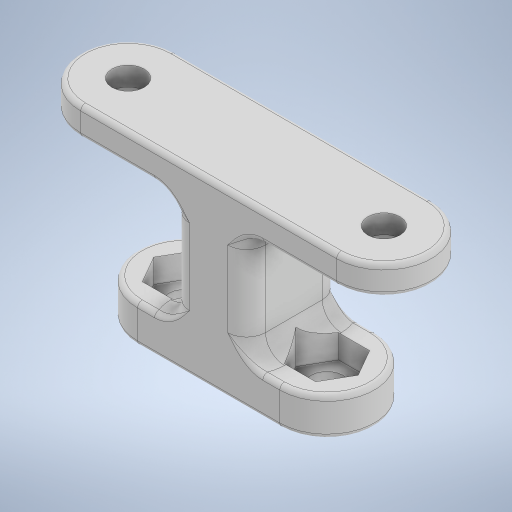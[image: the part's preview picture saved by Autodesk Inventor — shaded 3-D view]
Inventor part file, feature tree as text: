
AUTODESK INVENTOR PART (.ipt)
format: ipt  version: 2024.2 (Build 282272000, 272)  size: 422,912 bytes
history: native  units: mm
features: extrude x6, sketch x6, fillet x2
ambient origin geometry x8: Origin, YZ Plane, XZ Plane, XY Plane, X Axis, Y Axis, Z Axis, Center Point
bodies: Solid1 (feature_tree)
feature tree (14):
  extrude  "Extrusion1"  Depth=27.0mm
  extrude  "Extrusion2"  Depth=10.0mm TaperAngle=0.0deg
  extrude  "Extrusion3"  Depth=15.0mm
  extrude  "Extrusion4"  Depth=5.7mm
  extrude  "Extrusion5"  Depth=3.4mm
  extrude  "Extrusion6"  Depth=0.5mm
  fillet  "Fillet3"  Radius=1.0mm
  fillet  "Fillet2"  Radius=0.5mm
  sketch  "Sketch1"  dims[d0=3.4mm d1=27.0mm]
  sketch  "Sketch2"  dims[d2=10.0mm d3=3.0mm d4=0.0mm]
  sketch  "Sketch3"  dims[d5=12.0mm d6=0.0mm d7=15.0mm]
  sketch  "Sketch4"  dims[d8=4.0mm d9=0.0mm d10=5.7mm]
  sketch  "Sketch5"  dims[d11=2.5mm d12=0.0mm d13=3.4mm]
  sketch  "Sketch6"  dims[d14=2.0mm d15=0.0mm d16=5.1mm d17=1.0mm d18=0.0mm d20=0.5mm d22=8.0mm d23=2.0mm]
